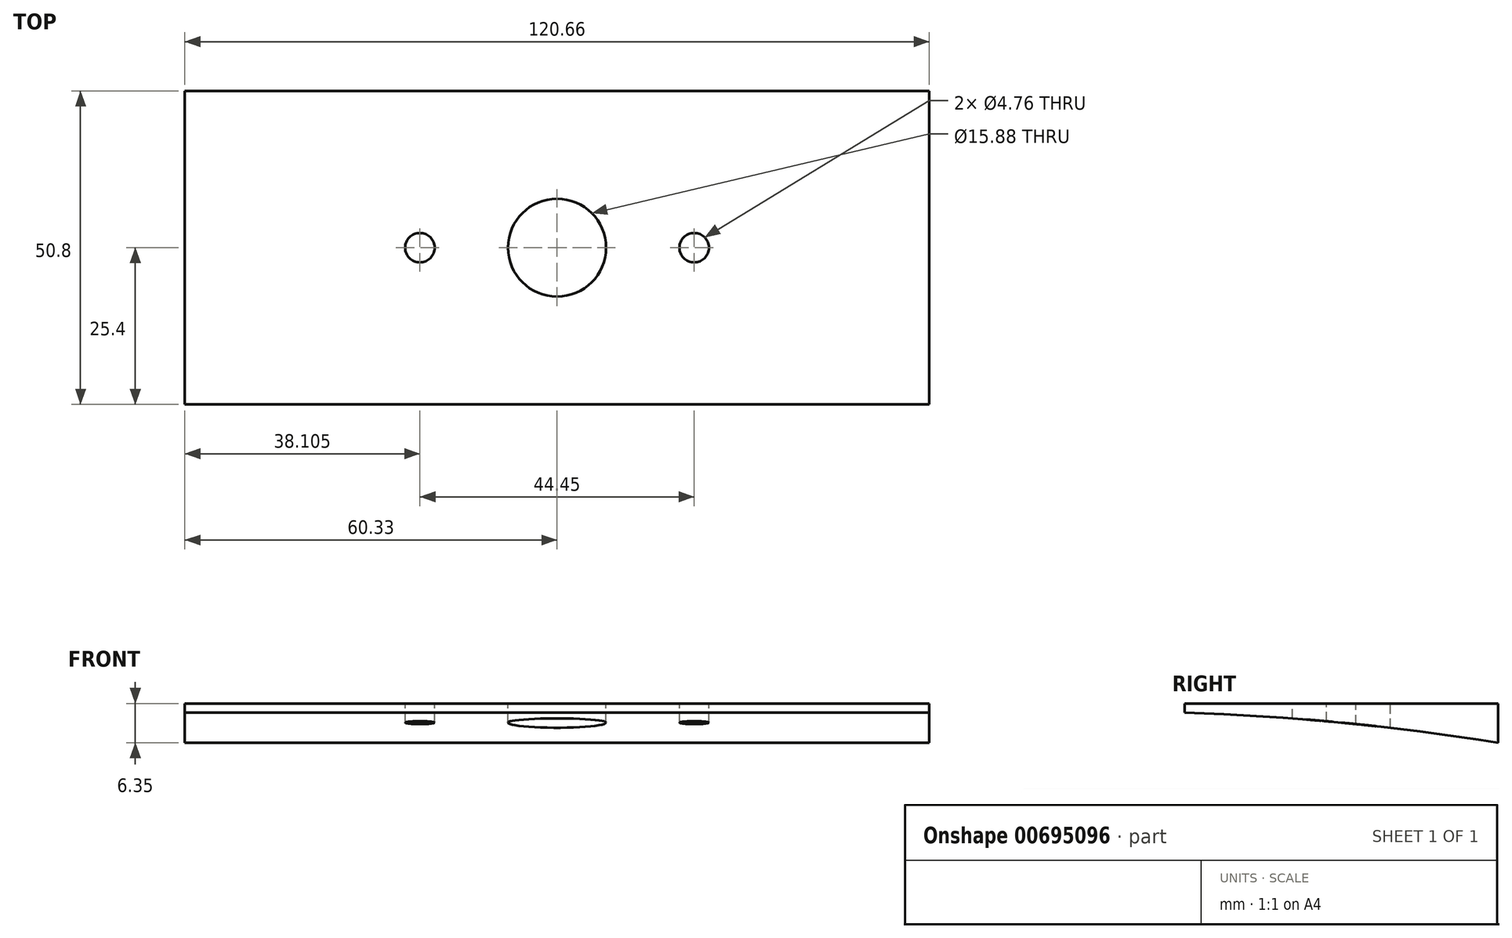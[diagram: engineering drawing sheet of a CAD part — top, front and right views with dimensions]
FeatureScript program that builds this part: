
annotation { "Feature Type Name" : "Feature", "Feature Type Description" : "" }
export const myFeature = defineFeature(function(context is Context, id is Id, definition is map)
    precondition{}
    {
        {
            var Q0;
            Q0=qCreatedBy(makeId("Right.planeOp"),FACE);
            var sketch = newSketch(context, id + "F0", { "sketchPlane" : qUnion([Q0])});
            skLineSegment(sketch, "E0.top", {"start": v(0, 6.35) * mm, "end": v(-50.8, 6.35) * mm});
            skLineSegment(sketch, "E0.left", {"start": v(0, 0) * mm, "end": v(0, 6.35) * mm});
            skLineSegment(sketch, "E0.right", {"start": v(-50.8, 4.87) * mm, "end": v(-50.8, 6.35) * mm});
            skCircle(sketch, "E1", {"center": v(0, 0) * mm, "radius": 63.5 * mm, "construction": true});
            skCircle(sketch, "E2", {"center": v(-63.5, 0) * mm, "radius": 400.05 * mm, "construction": true});
            skLineSegment(sketch, "E3", {"start": v(-63.5, 0) * mm, "end": v(-63.5, -400.05) * mm, "construction": true});
            skArc(sketch, "E4", {"start": v(-373.81, -142.5) * mm, "mid": v(-96.8, -793.64) * mm, "end": v(284.4, -197.49) * mm});
            skArc(sketch, "E5.trimOffspring", {"start": v(0, 0) * mm, "mid": v(-25.32, 3.25) * mm, "end": v(-50.8, 4.87) * mm});
            skSolve(sketch);
        }
        {
            var Q0;
            Q0=makeQuery(id+"F0.imprint","IMPRINT",FACE,{"disambiguationData":[TD([[makeQuery(id+"F0.imprint","IMPRINT",EDGE,{"derivedFrom":sQuery(id+"F0.wireOp",EDGE,"E0.top")}),1.0]])]});
            extrude(context, id + "F1", {"entities" : qUnion([Q0]), "depth" : 120.65 * mm, "offsetDistance" : 25.4 * mm, "symmetric" : true});
        }
        {
            var Q0;
            Q0=makeQuery(id+"F1.opExtrude","SWEPT_FACE",FACE,{"disambiguationData":[OSD([sQuery(id+"F0.wireOp",EDGE,"E0.top")])]});
            var sketch = newSketch(context, id + "F2", { "sketchPlane" : qUnion([Q0])});
            skLineSegment(sketch, "E6", {"start": v(0, 0) * mm, "end": v(0, -50.8) * mm, "construction": true});
            skPoint(sketch, "E7.endSnap0", {"position": v(0, -25.4) * mm});
            skLineSegment(sketch, "E8", {"start": v(60.34, -25.4) * mm, "end": v(-60.31, -25.4) * mm, "construction": true});
            skCircle(sketch, "E9", {"center": v(0, -25.4) * mm, "radius": 7.94 * mm});
            skCircle(sketch, "E10", {"center": v(0, -25.4) * mm, "radius": 22.23 * mm, "construction": true});
            skCircle(sketch, "E11", {"center": v(-22.23, -25.4) * mm, "radius": 2.38 * mm});
            skCircle(sketch, "E12", {"center": v(22.23, -25.4) * mm, "radius": 2.38 * mm});
            skSolve(sketch);
        }
        {
            var Q0;
            Q0 = qSketchRegion(id + "F2", true);
            var Q1;
            Q1=makeQuery(id+"F1.opExtrude","SWEPT_FACE",FACE,{"disambiguationData":[OSD([sQuery(id+"F0.wireOp",EDGE,"E5.trimOffspring")])]});
            extrude(context, id + "F3", {"entities" : qUnion([Q0]), "operationType" : NewBodyOperationType.REMOVE, "endBound" : BoundingType.UP_TO_SURFACE, "oppositeDirection" : true, "depth" : 25.4 * mm, "endBoundEntityFace" : qUnion([Q1]), "offsetDistance" : 25.4 * mm});
        }
    });
